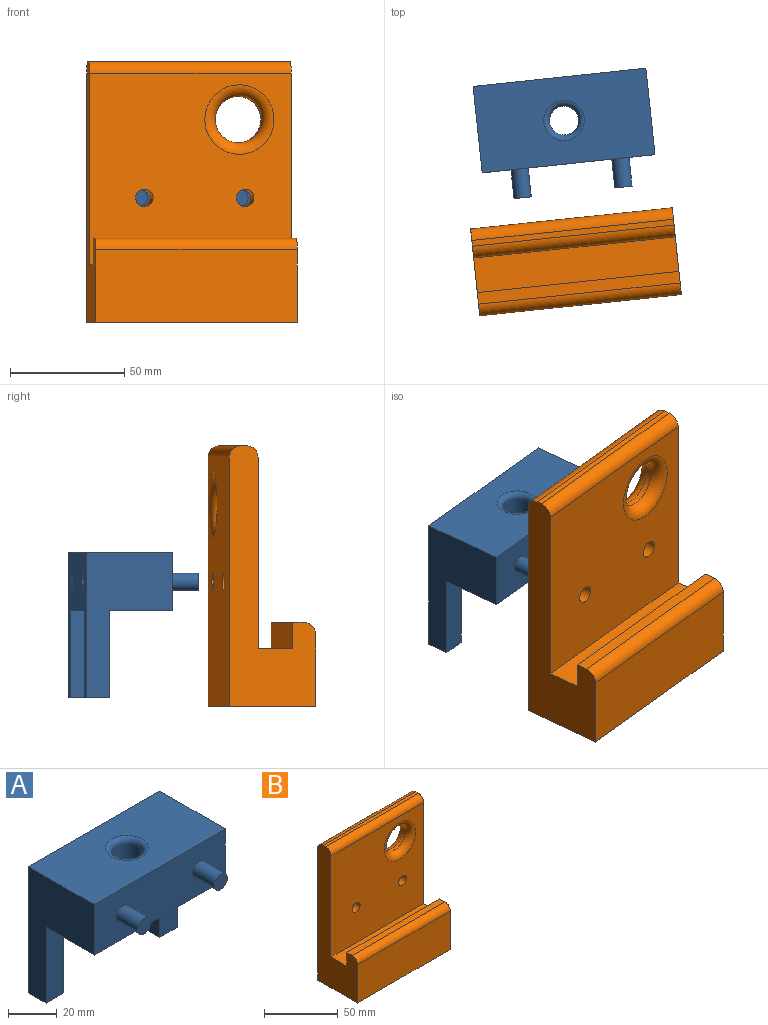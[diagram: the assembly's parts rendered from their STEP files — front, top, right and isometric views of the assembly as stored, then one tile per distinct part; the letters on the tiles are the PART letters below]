
ASSEMBLY  parts=2 mates=2
PART A: 23 faces, bbox 76.2x50.8x63.5 mm
  f0: plane 76.2x38.1mm, normal (0,0,-1), area 2448.5mm2, adj f1,f3,f4,f5,f11,f17,f18,f20
  f1: plane 63.5x38.1mm, normal (1,0,0), area 1354.8mm2, adj f0,f2,f4,f5,f20,f22
  f2: plane 76.2x38.1mm, normal (0,0,1), area 2654.9mm2, adj f1,f3,f4,f5,f12
  f3: plane 63.5x38.1mm, normal (-1,0,0), area 1354.8mm2, adj f0,f2,f4,f5,f17,f19
  f4: plane 76.2x25.4mm, normal (0,-1,0), area 1844.3mm2, adj f0,f1,f2,f3,f6,f8
  f5: plane 76.2x63.5mm, normal (0,1,0), area 2618.5mm2, adj f0,f1,f2,f3,f14,f16,f18,f19
  f6: cylinder r=3.81mm len=12.7mm, axis (0,1,0), area 304mm2, adj f4,f7
  f7: plane 7.62x7.62mm, normal (0,-1,0), area 45.6mm2, adj f6
  f8: cylinder r=3.81mm len=12.7mm, axis (0,1,0), area 304mm2, adj f4,f9
  f9: plane 7.62x7.62mm, normal (0,-1,0), area 45.6mm2, adj f8
  f10: cylinder r=6.35mm len=20.32mm, axis (0,0,1), area 810.7mm2, adj f11,f12
  f11: torus R=8.89mm, axis (0,0,-1), area 182.3mm2, adj f0,f10
  f12: torus R=8.89mm, axis (0,0,-1), area 182.3mm2, adj f2,f10
  f13: cone r=0mm half-angle=59deg, axis (0,1,0), area 53.2mm2, adj f14
  f14: cylinder r=3.81mm len=29.21mm, axis (0,1,0), area 699.3mm2, adj f5,f13
  f15: cone r=0mm half-angle=59deg, axis (0,1,0), area 53.2mm2, adj f16
  f16: cylinder r=3.81mm len=29.21mm, axis (0,1,0), area 699.3mm2, adj f5,f15
  f17: plane 38.1x10.16mm, normal (0,-1,0), area 387.1mm2, adj f0,f3,f18,f19
  f18: plane 38.1x10.16mm, normal (1,0,0), area 387.1mm2, adj f0,f5,f17,f19
  f19: plane 10.16x10.16mm, normal (0,0,-1), area 103.2mm2, adj f3,f5,f17,f18
  f20: plane 38.1x10.16mm, normal (0,-1,0), area 387.1mm2, adj f0,f1,f21,f22
  f21: plane 38.1x10.16mm, normal (-1,0,0), area 387.1mm2, adj f0,f5,f20,f22
  f22: plane 10.16x10.16mm, normal (0,0,-1), area 103.2mm2, adj f1,f5,f20,f21
PART B: 18 faces, bbox 88.9x38.1x114.3 mm
  f0: plane 88.9x15.24mm, normal (0,0,1), area 1354.8mm2, adj f1,f7,f8,f9
  f1: plane 88.9x11.43mm, normal (0,1,0), area 1016.1mm2, adj f0,f2,f8,f9
  f2: plane 88.9x5.08mm, normal (0,0,1), area 451.6mm2, adj f1,f8,f9,f11
  f3: plane 88.9x31.75mm, normal (0,-1,0), area 2822.6mm2, adj f4,f8,f9,f11
  f4: plane 88.9x38.1mm, normal (0,0,-1), area 3387.1mm2, adj f3,f5,f8,f9
  f5: plane 109.22x88.9mm, normal (0,1,0), area 8888.8mm2, adj f4,f8,f9,f12,f14,f16,f17
  f6: plane 88.9x2.54mm, normal (0,0,1), area 225.8mm2, adj f8,f9,f12,f13
  f7: plane 88.9x83.82mm, normal (0,-1,0), area 6630.7mm2, adj f0,f8,f9,f13,f15,f16,f17
  f8: plane 114.3x38.1mm, normal (-1,0,0), area 2196.3mm2, adj f0,f1,f2,f3,f4,f5,f6,f7
  f9: plane 114.3x38.1mm, normal (1,0,0), area 2196.3mm2, adj f0,f1,f2,f3,f4,f5,f6,f7
  f10: cylinder r=10.16mm len=20.32mm, axis (0,-1,0), area 162.1mm2, adj f14,f15
  f11: cylinder r=5.08mm len=88.9mm, axis (1,0,0), area 709.4mm2, adj f2,f3,f8,f9
  f12: cylinder r=5.08mm len=88.9mm, axis (1,0,0), area 709.4mm2, adj f5,f6,f8,f9
  f13: cylinder r=5.08mm len=88.9mm, axis (1,0,0), area 709.4mm2, adj f6,f7,f8,f9
  f14: torus R=15.24mm, axis (0,-1,0), area 602mm2, adj f5,f10
  f15: torus R=15.24mm, axis (0,1,0), area 602mm2, adj f7,f10
  f16: cylinder r=3.81mm len=12.7mm, axis (0,1,0), area 304mm2, adj f5,f7
  f17: cylinder r=3.81mm len=12.7mm, axis (0,1,0), area 304mm2, adj f5,f7
PLACE A rot(axis=(0,0,1),6deg) t=(35.79,16.36,-230.45)mm
PLACE B rot(axis=(0,0,1),6deg) t=(50.27,-72.69,-246.96)mm
MATE slider A.f8 <-> B.f17  axis (0.1,-0.99,0) through (25.95,-35.75,-217.75)mm
MATE parallel A.f8 <-> B.f17  axis (0.1,-0.99,0) through (25.95,-35.75,-217.75)mm
